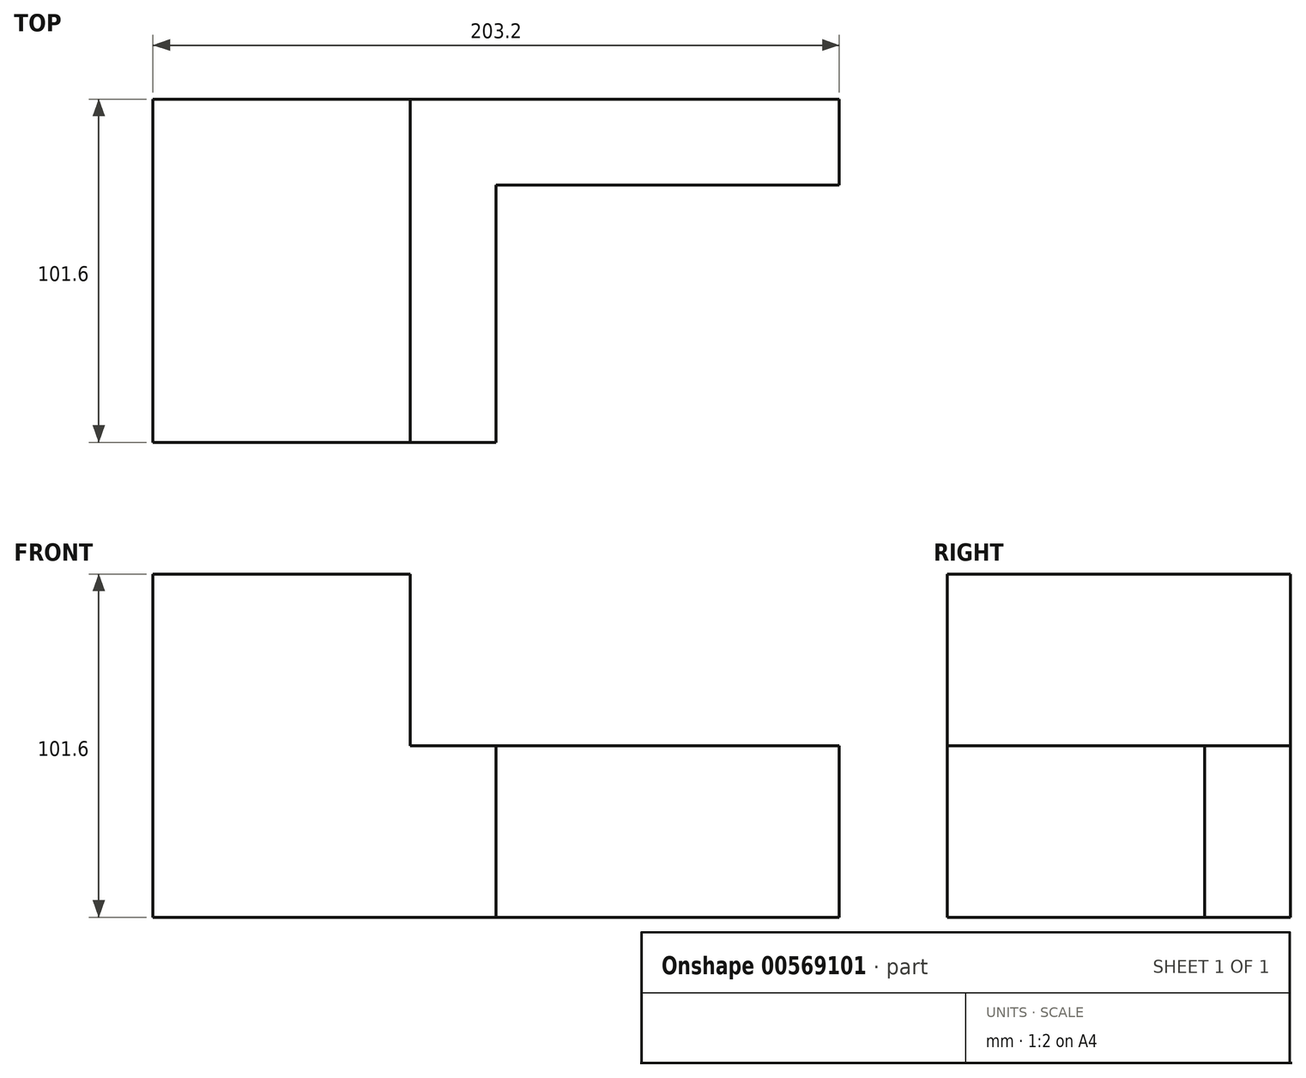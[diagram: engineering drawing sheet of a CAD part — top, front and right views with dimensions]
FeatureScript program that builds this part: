
annotation { "Feature Type Name" : "Feature", "Feature Type Description" : "" }
export const myFeature = defineFeature(function(context is Context, id is Id, definition is map)
    precondition{}
    {
        {
            var Q0;
            Q0=qCreatedBy(makeId("Front.planeOp"),FACE);
            var sketch = newSketch(context, id + "F0", { "sketchPlane" : qUnion([Q0])});
            skLineSegment(sketch, "E0.bottom", {"start": v(0, -50.8) * mm, "end": v(-76.2, -50.8) * mm});
            skLineSegment(sketch, "E0.top", {"start": v(0, 50.8) * mm, "end": v(-76.2, 50.8) * mm});
            skLineSegment(sketch, "E0.left", {"start": v(0, -50.8) * mm, "end": v(0, 50.8) * mm});
            skLineSegment(sketch, "E0.right", {"start": v(-76.2, -50.8) * mm, "end": v(-76.2, 50.8) * mm});
            skPoint(sketch, "E0.middle", {"position": v(-38.1, 0) * mm});
            skLineSegment(sketch, "E1", {"start": v(0, -50.8) * mm, "end": v(25.4, -50.8) * mm});
            skLineSegment(sketch, "E2", {"start": v(25.4, -50.8) * mm, "end": v(25.4, 0) * mm});
            skLineSegment(sketch, "E3", {"start": v(25.4, 0) * mm, "end": v(0, 0) * mm});
            skSolve(sketch);
        }
        {
            var Q0;
            Q0=qSketchRegion(id+"F0",true);
            extrude(context, id + "F1", {"entities" : qUnion([Q0]), "depth" : 101.6 * mm});
        }
        {
            var Q0;
            Q0=makeQuery(id+"F1.opExtrude","SWEPT_FACE",FACE,{"disambiguationData":[OSD([sQuery(id+"F0.wireOp",EDGE,"E2")])]});
            var sketch = newSketch(context, id + "F2", { "sketchPlane" : qUnion([Q0])});
            skLineSegment(sketch, "E4.bottom", {"start": v(0, 0) * mm, "end": v(-25.4, 0) * mm});
            skLineSegment(sketch, "E4.top", {"start": v(0, -50.8) * mm, "end": v(-25.4, -50.8) * mm});
            skLineSegment(sketch, "E4.left", {"start": v(0, 0) * mm, "end": v(0, -50.8) * mm});
            skLineSegment(sketch, "E4.right", {"start": v(-25.4, 0) * mm, "end": v(-25.4, -50.8) * mm});
            skSolve(sketch);
        }
        {
            var Q0;
            Q0=qSketchRegion(id+"F0",true);
            extrude(context, id + "F3", {"entities" : qUnion([Q0]), "operationType" : NewBodyOperationType.ADD, "depth" : 8.64 * mm});
        }
        {
            var Q0;
            Q0=qSketchRegion(id+"F2",true);
            extrude(context, id + "F4", {"entities" : qUnion([Q0]), "operationType" : NewBodyOperationType.ADD, "depth" : 101.6 * mm});
        }
    });
